# Revit family: Maxlogic Intelligent Addressable GCU (GateWay Control Unit)
name_source: partatom
category: Fire Alarm Devices
units: mm (PartAtom-declared; Revit-internal decimal feet)

## family parameters
Cut with Voids When Loaded = No
Host = Face
Maintain Annotation Orientation = Yes
OmniClass Number = 23.85.30.21
OmniClass Title = Environmental Detection/Registration
Part Type = Normal
Room Calculation Point = No
Round Connector Dimension = Use Diameter
Shared = No

## types (7) — shared parameters
Battery = 2 X (12V DC 7 Ah )
Color = White
External supply = 220 V AC
Fax Number = (+)90 216 466 45 10
Installation Manual = https://mavilielektronik.com
Main Material = Metal Grey
Manufacturer = Mavili Elektronik Ticaret A.Ş.
Model = Maxlogic
Mounting surface = Wall mount
Nominal Depth = 100 mm
Nominal Height = 300 mm
Nominal Width = 400 mm
Operating temperature = (-5°C) - (+50°C)
Secondary Material = White Plastic ABS
URL = https://www.mavili.com.tr
Warranty Duration Labor = 2
Warranty Duration Parts = 2
Warranty Duration Unit = Year
Weight = 6,200 kg
zero-valued in all types: Cost, Default Elevation

## per-type parameters (varying)
| type | Code Performance | Description | Product Code |
| Maxlogic Intelligent Addressable GCU module with 3A power supply, B type box, TCP/IP module included | EN 54-4 / EN 54-18 | Intelligent Addressable GCU module with 3A power supply, B type box, TCP/IP module included | ML-1207.C |
| Maxlogic Intelligent Addressable GCU module with 3A power supply, B type box, GPRS module included | EN 54-4 / EN 54-18 | Intelligent Addressable GCU module with 3A power supply, B type box, GPRS module included | ML-1207.G |
| Maxlogic Intelligent Addressable GCU module with 3A power supply, B type box, RS-232/RS-485 module included | EN 54-4 / EN 54-18 | Intelligent Addressable GCU module with 3A power supply, B type box, RS-232/RS-485 module included | ML-1207.K |
| Maxlogic Intelligent Addressable Modbus gcu module with 3A power supply, B type box | EN 54-4 / EN 54-18 | Intelligent Addressable Modbus gcu module with 3A power supply, B type box | ML-1207.MX |
| Maxlogic Intelligent Addressable GCU module with 3A power supply,TCP/IP, GPRS, RS-232/RS-485 module included | EN 54-4 / EN 54-18 | Intelligent Addressable GCU module with 3A power supply,TCP/IP, GPRS, RS-232/RS-485 module included | ML-1207.CGK |
| Maxlogic Intelligent Addressable GCU bacnet panel with 3A power supply, B type box | EN 54-4 / EN 54-18 | Intelligent Addressable GCU bacnet panel with 3A power supply, B type box | ML-1207.B |
| Maxlogic Intelligent Addressable NTP Server Communication Module |  | Intelligent Addressable NTP Server Communication Module | ML-1207.NTP |

## geometry (parser evidence)
native form markers: Sweep x2
no freeform markers — native parametric forms only
